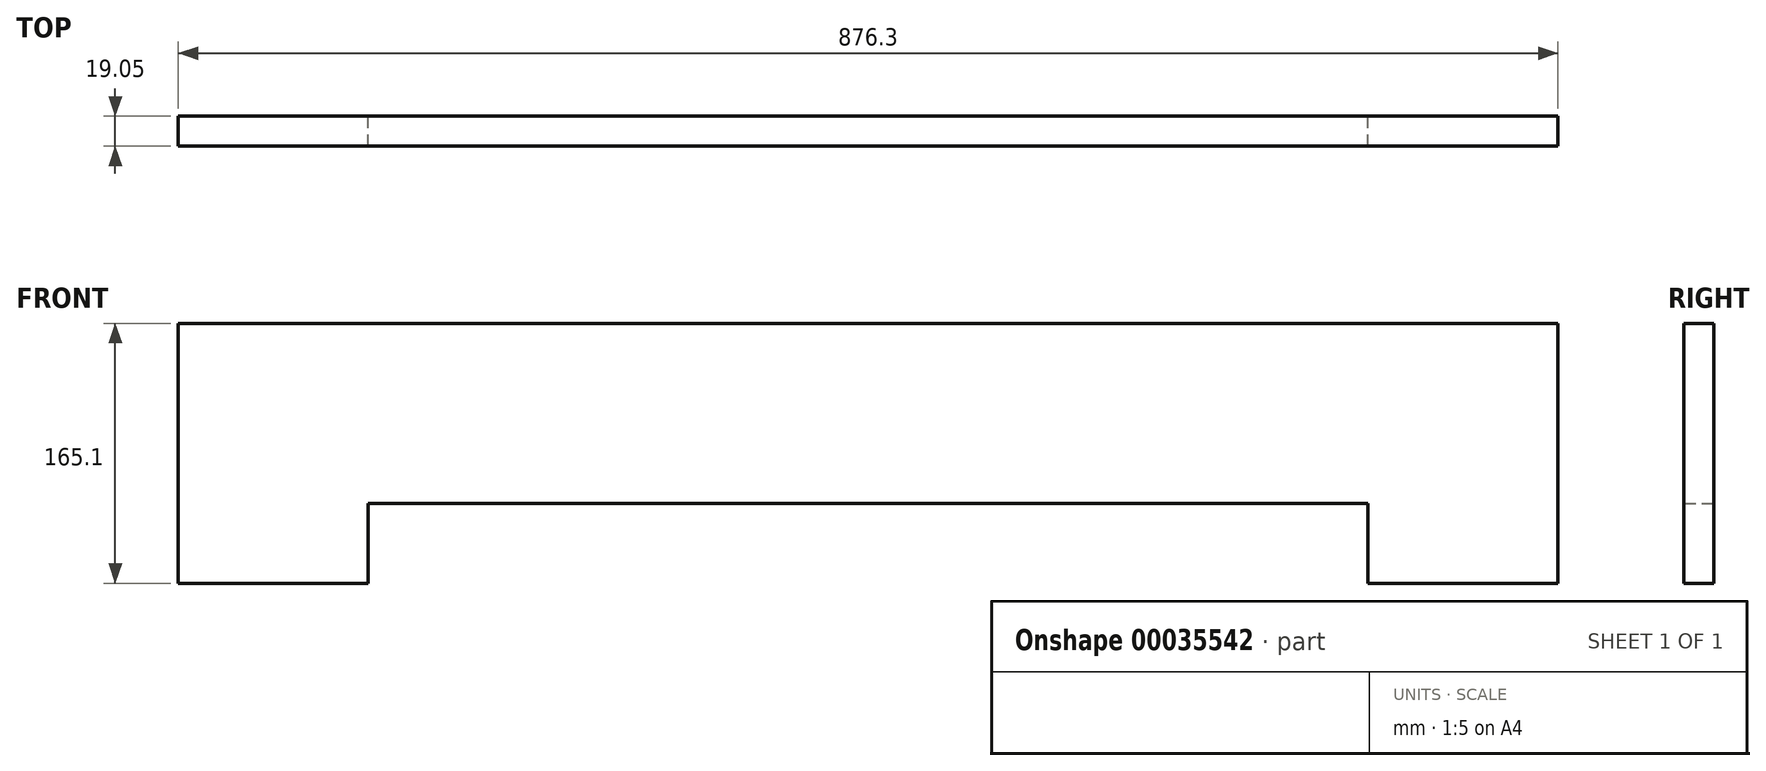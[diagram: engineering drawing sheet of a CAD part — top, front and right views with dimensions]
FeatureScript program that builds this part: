
annotation { "Feature Type Name" : "Feature", "Feature Type Description" : "" }
export const myFeature = defineFeature(function(context is Context, id is Id, definition is map)
    precondition{}
    {
        {
            var Q0;
            Q0=qCreatedBy(makeId("Front.planeOp"),FACE);
            var sketch = newSketch(context, id + "F0", { "sketchPlane" : qUnion([Q0])});
            skLineSegment(sketch, "E0.bottom", {"start": v(-440.04, 88.3) * mm, "end": v(436.26, 88.3) * mm});
            skLineSegment(sketch, "E0.top", {"start": v(-440.04, -76.8) * mm, "end": v(-319.39, -76.8) * mm});
            skLineSegment(sketch, "E0.left", {"start": v(-440.04, 88.3) * mm, "end": v(-440.04, -76.8) * mm});
            skLineSegment(sketch, "E0.right", {"start": v(436.26, 88.3) * mm, "end": v(436.26, -76.8) * mm});
            skLineSegment(sketch, "E1", {"start": v(-319.39, -76.8) * mm, "end": v(-319.39, -26) * mm});
            skLineSegment(sketch, "E2", {"start": v(-319.39, -26) * mm, "end": v(315.61, -26) * mm});
            skLineSegment(sketch, "E3", {"start": v(315.61, -26) * mm, "end": v(315.61, -76.8) * mm});
            skLineSegment(sketch, "E4.trimOffspring", {"start": v(315.61, -76.8) * mm, "end": v(436.26, -76.8) * mm});
            skSolve(sketch);
        }
        {
            var Q0;
            Q0 = qSketchRegion(id + "F0", true);
            extrude(context, id + "F1", {"entities" : qUnion([Q0]), "depth" : 19.05 * mm});
        }
    });
